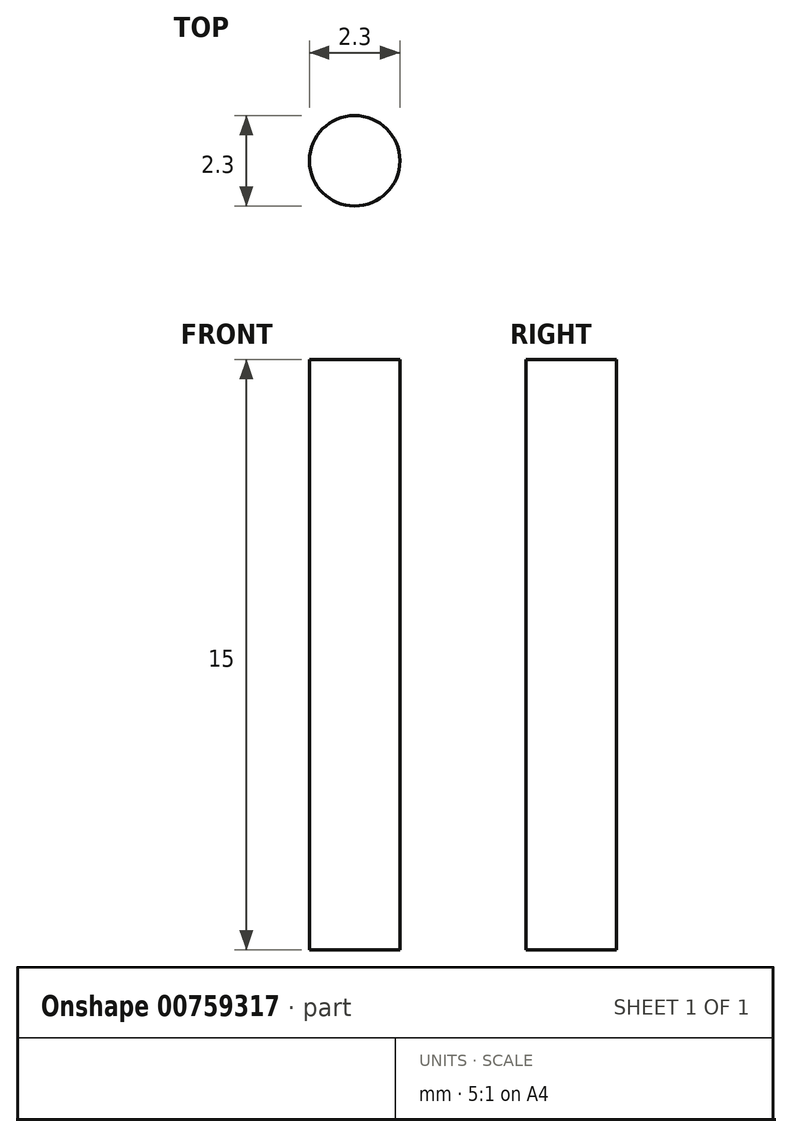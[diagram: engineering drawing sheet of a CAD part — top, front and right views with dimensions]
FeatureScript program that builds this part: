
annotation { "Feature Type Name" : "Feature", "Feature Type Description" : "" }
export const myFeature = defineFeature(function(context is Context, id is Id, definition is map)
    precondition{}
    {
        {
            var Q0;
            Q0=qCreatedBy(makeId("Top.planeOp"),FACE);
            var sketch = newSketch(context, id + "F0", { "sketchPlane" : qUnion([Q0])});
            skCircle(sketch, "E0", {"center": v(0, 0) * mm, "radius": 1.15 * mm});
            skSolve(sketch);
        }
        {
            var Q0;
            Q0=makeQuery(id+"F0.imprint","IMPRINT",FACE,{"disambiguationData":[TD([[makeQuery(id+"F0.imprint","IMPRINT",EDGE,{"derivedFrom":sQuery(id+"F0.wireOp",EDGE,"E0")}),1.0]])]});
            extrude(context, id + "F1", {"entities" : qUnion([Q0]), "depth" : 15 * mm, "offsetDistance" : 25 * mm});
        }
    });
